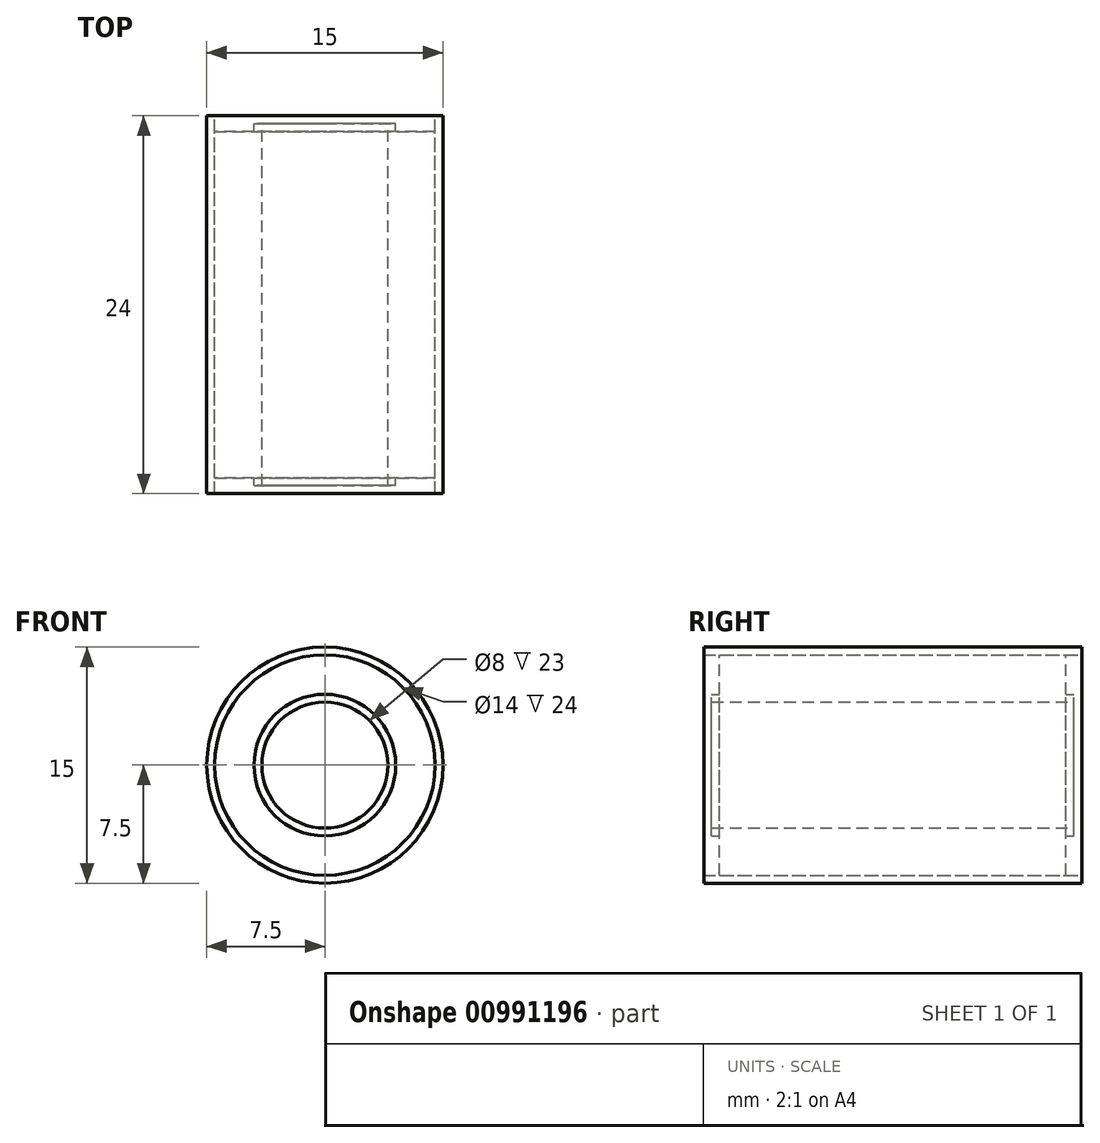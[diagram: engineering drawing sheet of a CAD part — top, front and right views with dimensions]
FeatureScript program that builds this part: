
annotation { "Feature Type Name" : "Feature", "Feature Type Description" : "" }
export const myFeature = defineFeature(function(context is Context, id is Id, definition is map)
    precondition{}
    {
        {
            var Q0;
            Q0=qCreatedBy(makeId("Front.planeOp"),FACE);
            var sketch = newSketch(context, id + "F0", { "sketchPlane" : qUnion([Q0])});
            skCircle(sketch, "E0", {"center": v(0, 0) * mm, "radius": 7.5 * mm});
            skCircle(sketch, "E1", {"center": v(0, 0) * mm, "radius": 7 * mm});
            skCircle(sketch, "E2", {"center": v(0, 0) * mm, "radius": 4 * mm});
            skCircle(sketch, "E3", {"center": v(0, 0) * mm, "radius": 4.5 * mm});
            skSolve(sketch);
        }
        {
            var Q0;
            Q0=makeQuery(id+"F0.imprint","IMPRINT",FACE,{"disambiguationData":[TD([[makeQuery(id+"F0.imprint","IMPRINT",EDGE,{"derivedFrom":sQuery(id+"F0.wireOp",EDGE,"E0")}),1.0]])]});
            extrude(context, id + "F1", {"entities" : qUnion([Q0]), "depth" : 24 * mm, "offsetDistance" : 25 * mm, "symmetric" : true});
        }
        {
            var Q0;
            Q0=makeQuery(id+"F0.imprint","IMPRINT",FACE,{"disambiguationData":[TD([[makeQuery(id+"F0.imprint","IMPRINT",EDGE,{"derivedFrom":sQuery(id+"F0.wireOp",EDGE,"E1")}),1.0]])]});
            extrude(context, id + "F2", {"entities" : qUnion([Q0]), "depth" : 22 * mm, "offsetDistance" : 25 * mm, "symmetric" : true});
        }
        {
            var Q0;
            Q0=makeQuery(id+"F0.imprint","IMPRINT",FACE,{"disambiguationData":[TD([[makeQuery(id+"F0.imprint","IMPRINT",EDGE,{"derivedFrom":sQuery(id+"F0.wireOp",EDGE,"E2")}),-1.0]])]});
            extrude(context, id + "F3", {"entities" : qUnion([Q0]), "operationType" : NewBodyOperationType.ADD, "depth" : 23 * mm, "offsetDistance" : 25 * mm, "symmetric" : true});
        }
    });
